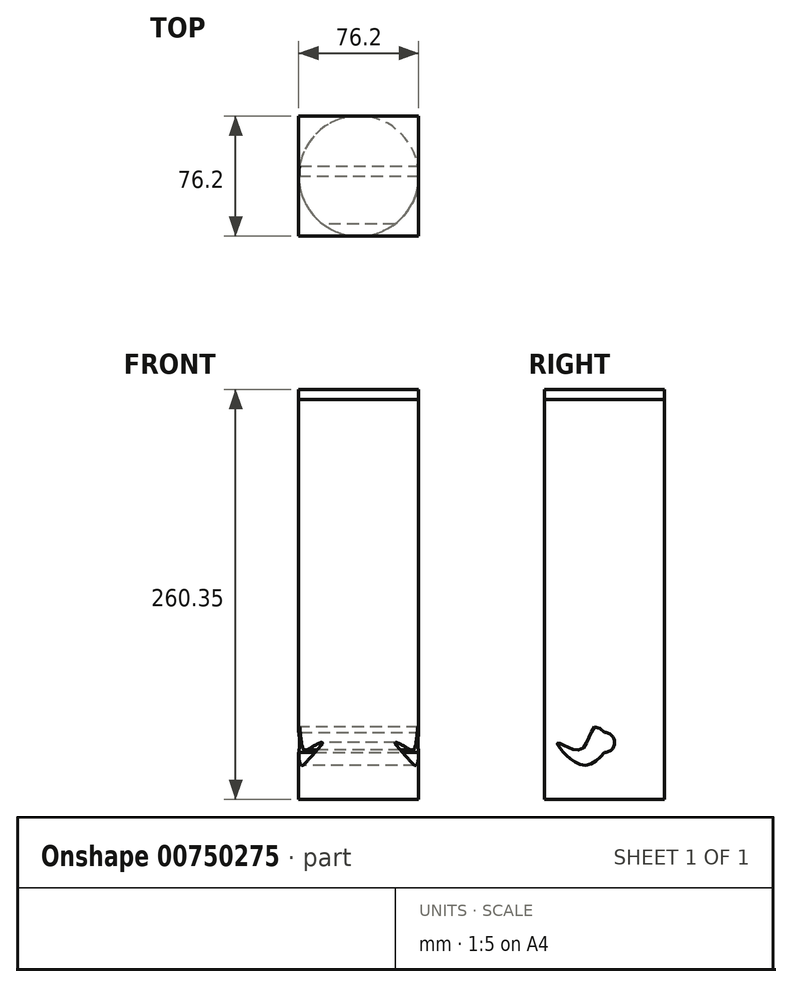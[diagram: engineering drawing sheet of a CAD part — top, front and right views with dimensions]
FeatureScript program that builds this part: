
annotation { "Feature Type Name" : "Feature", "Feature Type Description" : "" }
export const myFeature = defineFeature(function(context is Context, id is Id, definition is map)
    precondition{}
    {
        {
            var Q0;
            Q0=qCreatedBy(makeId("Top.planeOp"),FACE);
            var sketch = newSketch(context, id + "F0", { "sketchPlane" : qUnion([Q0])});
            skCircle(sketch, "E0", {"center": v(0, 0) * mm, "radius": 38.1 * mm});
            skSolve(sketch);
        }
        {
            var Q0;
            Q0 = qSketchRegion(id + "F0", true);
            extrude(context, id + "F1", {"entities" : qUnion([Q0]), "depth" : 254 * mm, "offsetDistance" : 25.4 * mm});
        }
        {
            var Q0;
            Q0=makeQuery(id+"F1.opExtrude","CAP_FACE",FACE,{"disambiguationData":[OSD([sQuery(id+"F0.wireOp",EDGE,"E0")])],"isStart":false});
            var sketch = newSketch(context, id + "F2", { "sketchPlane" : qUnion([Q0])});
            skLineSegment(sketch, "E1.bottom", {"start": v(-38.1, -38.1) * mm, "end": v(38.1, -38.1) * mm});
            skLineSegment(sketch, "E1.top", {"start": v(-38.1, 38.1) * mm, "end": v(38.1, 38.1) * mm});
            skLineSegment(sketch, "E1.left", {"start": v(-38.1, -38.1) * mm, "end": v(-38.1, 38.1) * mm});
            skLineSegment(sketch, "E1.right", {"start": v(38.1, -38.1) * mm, "end": v(38.1, 38.1) * mm});
            skPoint(sketch, "E1.middle", {"position": v(0, 0) * mm});
            skSolve(sketch);
        }
        {
            var Q0;
            Q0 = qSketchRegion(id + "F2", true);
            extrude(context, id + "F3", {"entities" : qUnion([Q0]), "operationType" : NewBodyOperationType.ADD, "depth" : 6.35 * mm, "offsetDistance" : 25.4 * mm});
        }
        {
            var Q0;
            Q0=qCreatedBy(makeId("Right.planeOp"),FACE);
            cPlane(context, id + "F4", {"entities" : qUnion([Q0]), "cplaneType" : CPlaneType.OFFSET, "offset" : 38.1 * mm, "width" : 152.4 * mm, "height" : 152.4 * mm});
        }
        {
            var Q0;
            Q0=qCreatedBy(id+"F4.planeOp",FACE);
            var sketch = newSketch(context, id + "F5", { "sketchPlane" : qUnion([Q0])});
            skArc(sketch, "E2", {"start": v(0, 29.82) * mm, "mid": v(6.35, 36.17) * mm, "end": v(0, 42.52) * mm});
            skFitSpline(sketch, "E3", {"points": [v(0, 29.82) * mm, v(-15.68, 22.2) * mm, v(-30.27, 36.17) * mm, v(-15.68, 31.51) * mm, v(-6.68, 45.8) * mm, v(0, 42.52) * mm], "startDerivative": vector(-64.85, -68.84) * mm, "endDerivative": vector(52.36, -50.03) * mm});
            skSolve(sketch);
        }
        {
            var Q0;
            Q0 = qSketchRegion(id + "F5", true);
            extrude(context, id + "F6", {"entities" : qUnion([Q0]), "operationType" : NewBodyOperationType.REMOVE, "endBound" : BoundingType.THROUGH_ALL, "oppositeDirection" : true, "depth" : 25.4 * mm, "offsetDistance" : 25.4 * mm});
        }
    });
